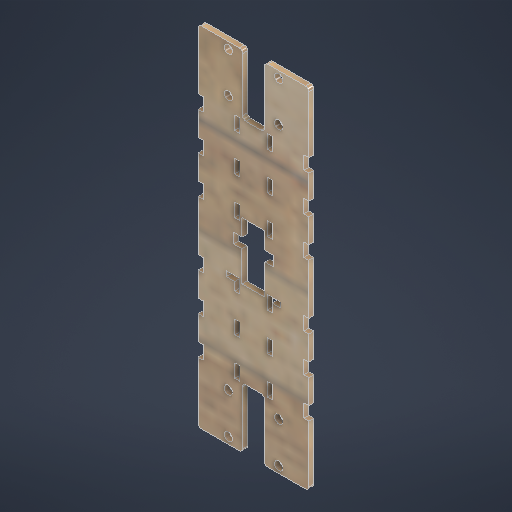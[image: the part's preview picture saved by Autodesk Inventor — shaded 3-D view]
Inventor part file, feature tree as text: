
AUTODESK INVENTOR PART (.ipt)
format: ipt  version: 2025.3 (Build 293356030, 356C)  size: 486,400 bytes
history: native  units: mm
features: sketch x3, other x2, extrude x2
ambient origin geometry x8: Origin, YZ Plane, XZ Plane, XY Plane, X Axis, Y Axis, Z Axis, Center Point
bodies: Body1 (feature_tree)
feature tree (7):
  other  "實體1"
  extrude  "擠出1"  Depth=66.0mm
  sketch  "草圖3"
  extrude  "擠出3"  Depth=208.0mm
  sketch  "草圖1"
  other  "草圖 - 矩形陣列1"
  sketch  "草圖4"
